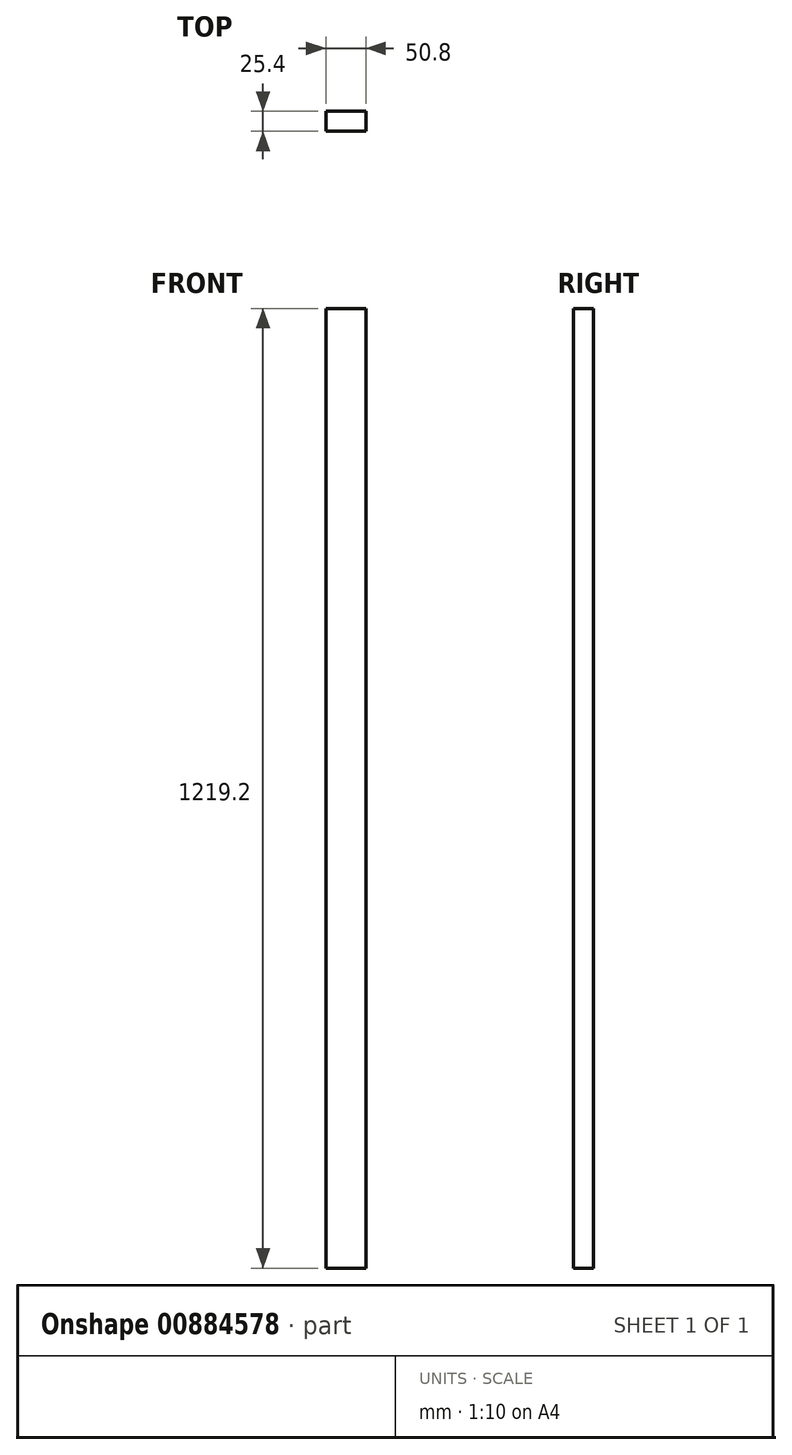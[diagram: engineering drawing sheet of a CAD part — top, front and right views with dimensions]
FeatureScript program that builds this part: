
annotation { "Feature Type Name" : "Feature", "Feature Type Description" : "" }
export const myFeature = defineFeature(function(context is Context, id is Id, definition is map)
    precondition{}
    {
        {
            var Q0;
            Q0=qCreatedBy(makeId("Front.planeOp"),FACE);
            var sketch = newSketch(context, id + "F0", { "sketchPlane" : qUnion([Q0])});
            skLineSegment(sketch, "E0.bottom", {"start": v(-18.39, 0) * mm, "end": v(32.41, 0) * mm});
            skLineSegment(sketch, "E0.top", {"start": v(-18.39, 1219.2) * mm, "end": v(32.41, 1219.2) * mm});
            skLineSegment(sketch, "E0.left", {"start": v(-18.39, 0) * mm, "end": v(-18.39, 1219.2) * mm});
            skLineSegment(sketch, "E0.right", {"start": v(32.41, 0) * mm, "end": v(32.41, 1219.2) * mm});
            skSolve(sketch);
        }
        {
            var Q0;
            Q0 = qSketchRegion(id + "F0", true);
            extrude(context, id + "F1", {"entities" : qUnion([Q0]), "depth" : 25.4 * mm, "offsetDistance" : 25.4 * mm});
        }
    });
